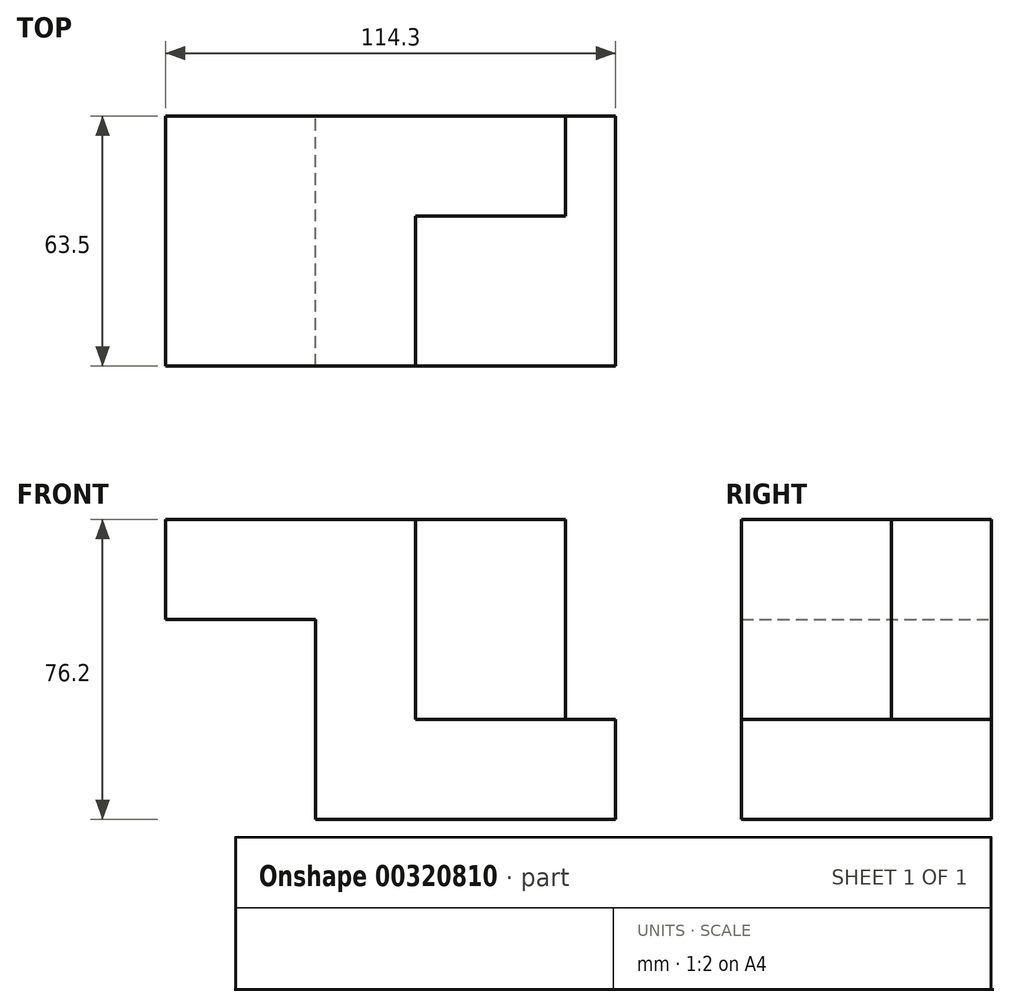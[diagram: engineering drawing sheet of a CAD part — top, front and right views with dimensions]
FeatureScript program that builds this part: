
annotation { "Feature Type Name" : "Feature", "Feature Type Description" : "" }
export const myFeature = defineFeature(function(context is Context, id is Id, definition is map)
    precondition{}
    {
        {
            var Q0;
            Q0=qCreatedBy(makeId("Front.planeOp"),FACE);
            var sketch = newSketch(context, id + "F0", { "sketchPlane" : qUnion([Q0])});
            skLineSegment(sketch, "E0", {"start": v(-57.5, 59.25) * mm, "end": v(-57.5, 33.85) * mm});
            skLineSegment(sketch, "E1", {"start": v(-57.5, 33.85) * mm, "end": v(-19.4, 33.85) * mm});
            skLineSegment(sketch, "E2", {"start": v(-19.4, 33.85) * mm, "end": v(-19.4, -16.95) * mm});
            skLineSegment(sketch, "E3", {"start": v(-19.4, -16.95) * mm, "end": v(56.8, -16.95) * mm});
            skLineSegment(sketch, "E4", {"start": v(56.8, -16.95) * mm, "end": v(56.8, 8.45) * mm});
            skLineSegment(sketch, "E5", {"start": v(56.8, 8.45) * mm, "end": v(6, 8.45) * mm});
            skLineSegment(sketch, "E6", {"start": v(6, 8.45) * mm, "end": v(6, 59.25) * mm});
            skLineSegment(sketch, "E7", {"start": v(6, 59.25) * mm, "end": v(-57.5, 59.25) * mm});
            skSolve(sketch);
        }
        {
            var Q0;
            Q0 = qSketchRegion(id + "F0", true);
            extrude(context, id + "F1", {"entities" : qUnion([Q0]), "depth" : 63.5 * mm});
        }
        {
            var Q0;
            Q0=makeQuery(id+"F1.opExtrude","CAP_FACE",FACE,{"disambiguationData":[OSD([sQuery(id+"F0.wireOp",EDGE,"E0"),sQuery(id+"F0.wireOp",EDGE,"E1"),sQuery(id+"F0.wireOp",EDGE,"E2"),sQuery(id+"F0.wireOp",EDGE,"E3"),sQuery(id+"F0.wireOp",EDGE,"E4"),sQuery(id+"F0.wireOp",EDGE,"E5"),sQuery(id+"F0.wireOp",EDGE,"E6"),sQuery(id+"F0.wireOp",EDGE,"E7")])],"isStart":true});
            var sketch = newSketch(context, id + "F2", { "sketchPlane" : qUnion([Q0])});
            skLineSegment(sketch, "E8", {"start": v(-6, 8.45) * mm, "end": v(-44.1, 8.45) * mm});
            skLineSegment(sketch, "E9", {"start": v(-44.1, 8.45) * mm, "end": v(-44.1, 59.25) * mm});
            skLineSegment(sketch, "E10", {"start": v(-44.1, 59.25) * mm, "end": v(-6, 59.25) * mm});
            skLineSegment(sketch, "E11", {"start": v(-6, 59.25) * mm, "end": v(-6, 8.45) * mm});
            skSolve(sketch);
        }
        {
            var Q0;
            Q0 = qSketchRegion(id + "F2", true);
            extrude(context, id + "F3", {"entities" : qUnion([Q0]), "operationType" : NewBodyOperationType.ADD, "oppositeDirection" : true, "depth" : 25.4 * mm});
        }
    });
